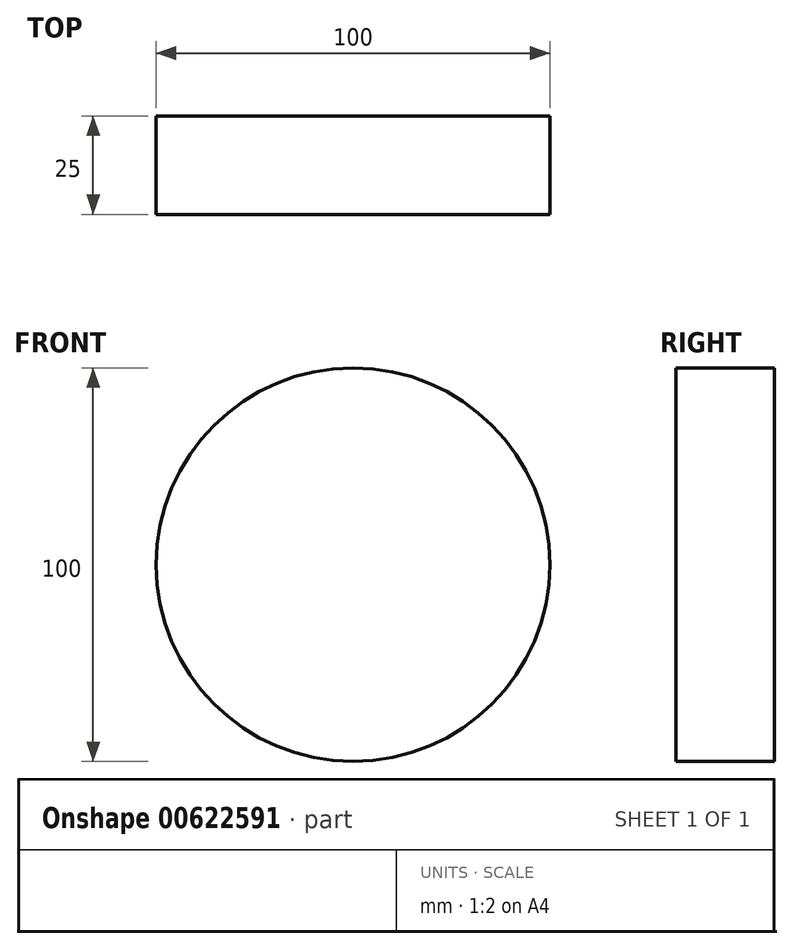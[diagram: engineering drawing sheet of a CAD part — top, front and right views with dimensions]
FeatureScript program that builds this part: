
annotation { "Feature Type Name" : "Feature", "Feature Type Description" : "" }
export const myFeature = defineFeature(function(context is Context, id is Id, definition is map)
    precondition{}
    {
        {
            var Q0;
            Q0=qCreatedBy(makeId("Front.planeOp"),FACE);
            var sketch = newSketch(context, id + "F0", { "sketchPlane" : qUnion([Q0])});
            skCircle(sketch, "E0", {"center": v(0, 0) * mm, "radius": 50 * mm});
            skSolve(sketch);
        }
        {
            var Q0;
            Q0 = qSketchRegion(id + "F0", true);
            extrude(context, id + "F1", {"entities" : qUnion([Q0]), "depth" : 25 * mm, "offsetDistance" : 25 * mm});
        }
    });
